# Revit family: Legrand Marina glass door references 036927 to 036974
name_source: partatom
category: Installations électriques
revit_build: Autodesk Revit 2018 (Build: 20170223_1515(x64)
units: mm (PartAtom-declared; Revit-internal decimal feet)

## family parameters
Basée sur le plan de construction = Non
Conserver l'orientation des annotations = Non
Cote de connecteur circulaire = Utiliser le diamètre
Couper avec des vides une fois chargée = Non
Numéro OmniClass = 23.80.00.00
Partagée = Non
Point de calcul de pièce = Non
Titre OmniClass = Electric Power and Lighting
Toujours verticalement = Oui
Type d'élément = Normal

## types (12) — shared parameters
ETIM Class = EC000058
Fabricant = Legrand
General Conditions of Use = https://export.legrand.com
Glass door = Oui
Horizontal version = Non
IK = 10
IP = 66
Material = Metallic
Number of door = 1
RAL = 7035
URL = www.legrand.fr

## per-type parameters (varying)
| type | Cabinet 036927 | Cabinet 036928 | Cabinet 036929 | Cabinet 036936 | Cabinet 036940 | Cabinet 036941 | Cabinet 036947 | Cabinet 036948 | Cabinet 036949 | Cabinet 036956 | Cabinet 036960 | Cabinet 036974 | Length | Square version | Vertical version | depth | height | weight |
| Legrand Atlantic 036927 | Oui | Non | Non | Non | Non | Non | Non | Non | Non | Non | Non | Non | 300 mm  [stored 0.984252 ft] | Non | Oui | 200 mm  [stored 0.656168 ft] | 400 mm  [stored 1.31234 ft] | 6.90 kg |
| Legrand Atlantic 036928 | Non | Oui | Non | Non | Non | Non | Non | Non | Non | Non | Non | Non | 400 mm  [stored 1.31234 ft] | Non | Oui | 200 mm  [stored 0.656168 ft] | 500 mm  [stored 1.64042 ft] | 11.20 kg |
| Legrand Atlantic 036929 | Non | Non | Oui | Non | Non | Non | Non | Non | Non | Non | Non | Non | 400 mm  [stored 1.31234 ft] | Non | Oui | 200 mm  [stored 0.656168 ft] | 600 mm | 13.00 kg |
| Legrand Atlantic 036936 | Non | Non | Non | Oui | Non | Non | Non | Non | Non | Non | Non | Non | 400 mm  [stored 1.31234 ft] | Non | Oui | 250 mm  [stored 0.82021 ft] | 600 mm | 14.00 kg |
| Legrand Atlantic 036940 | Non | Non | Non | Non | Oui | Non | Non | Non | Non | Non | Non | Non | 500 mm  [stored 1.64042 ft] | Non | Oui | 250 mm  [stored 0.82021 ft] | 700 mm  [stored 2.29659 ft] | 23.80 kg |
| Legrand Atlantic 036941 | Non | Non | Non | Non | Non | Oui | Non | Non | Non | Non | Non | Non | 600 mm | Non | Oui | 250 mm  [stored 0.82021 ft] | 800 mm  [stored 2.62467 ft] | 30.90 kg |
| Legrand Atlantic 036947 | Non | Non | Non | Non | Non | Non | Oui | Non | Non | Non | Non | Non | 600 mm | Non | Oui | 300 mm  [stored 0.984252 ft] | 800 mm  [stored 2.62467 ft] | 32.00 kg |
| Legrand Atlantic 036948 | Non | Non | Non | Non | Non | Non | Non | Oui | Non | Non | Non | Non | 600 mm | Non | Oui | 300 mm  [stored 0.984252 ft] | 1000 mm  [stored 3.28084 ft] | 45.00 kg |
| Legrand Atlantic 036949 | Non | Non | Non | Non | Non | Non | Non | Non | Oui | Non | Non | Non | 800 mm  [stored 2.62467 ft] | Non | Oui | 300 mm  [stored 0.984252 ft] | 1000 mm  [stored 3.28084 ft] | 56.90 kg |
| Legrand Atlantic 036956 | Non | Non | Non | Non | Non | Non | Non | Non | Non | Oui | Non | Non | 800 mm  [stored 2.62467 ft] | Non | Oui | 400 mm  [stored 1.31234 ft] | 1200 mm | 73.60 kg |
| Legrand Atlantic 036960 | Non | Non | Non | Non | Non | Non | Non | Non | Non | Non | Oui | Non | 800 mm  [stored 2.62467 ft] | Non | Oui | 400 mm  [stored 1.31234 ft] | 1400 mm  [stored 4.59318 ft] | 81.60 kg |
| Legrand Atlantic 036974 | Non | Non | Non | Non | Non | Non | Non | Non | Non | Non | Non | Oui | 600 mm | Oui | Non | 250 mm  [stored 0.82021 ft] | 600 mm | 22.80 kg |

note: [stored X ft] marks values corroborated as IEEE doubles in the binary element streams (Revit-internal decimal feet)
